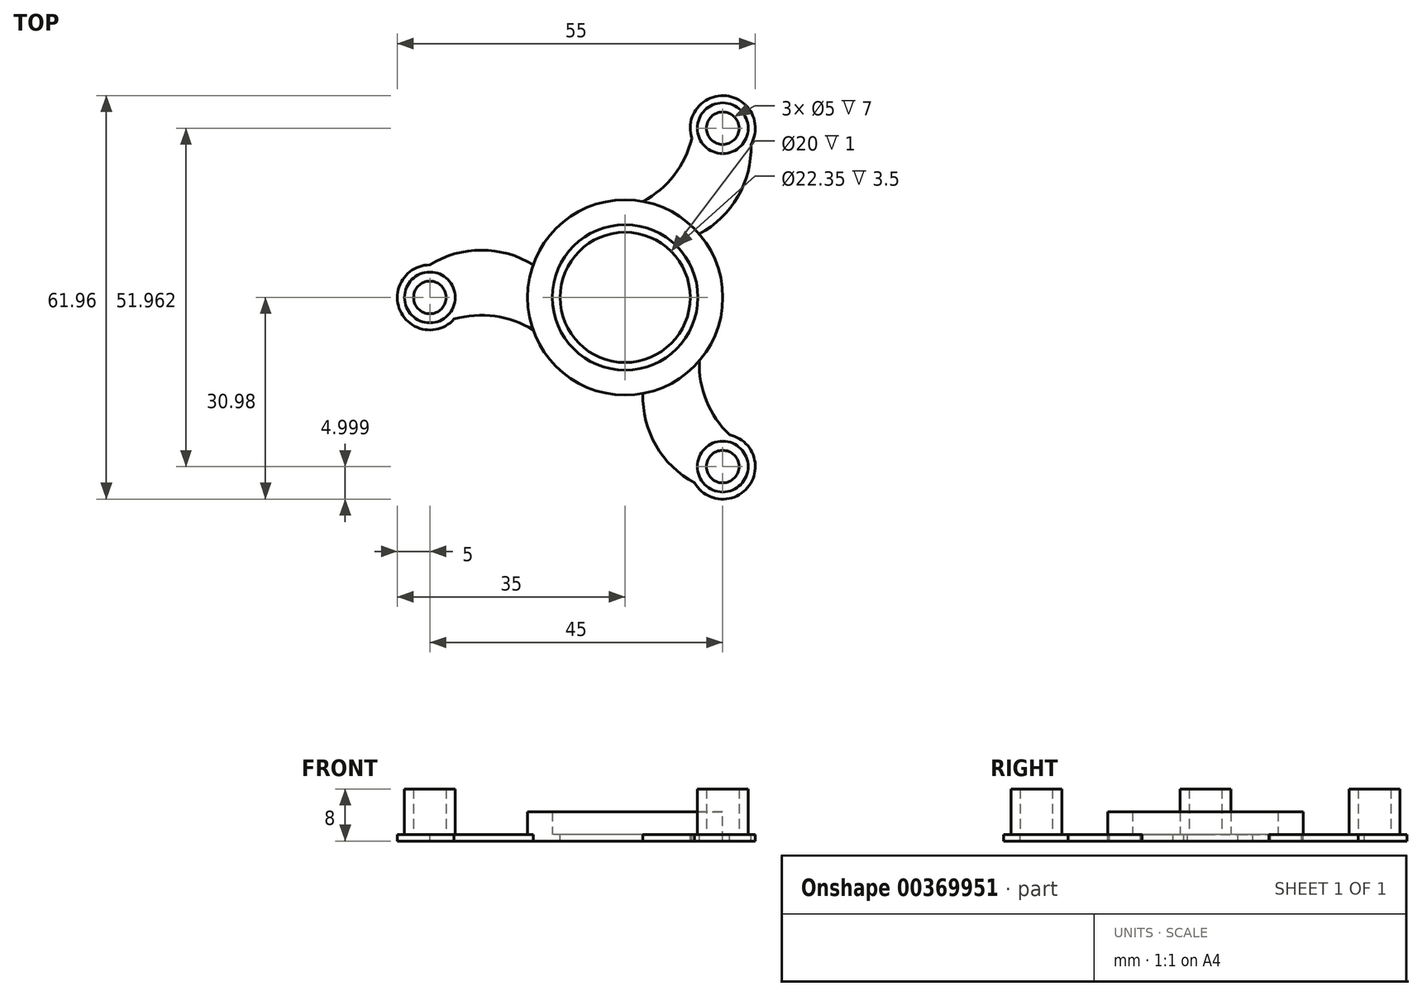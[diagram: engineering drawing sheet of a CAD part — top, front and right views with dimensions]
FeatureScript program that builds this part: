
annotation { "Feature Type Name" : "Feature", "Feature Type Description" : "" }
export const myFeature = defineFeature(function(context is Context, id is Id, definition is map)
    precondition{}
    {
        {
            var Q0;
            Q0=qCreatedBy(makeId("Top.planeOp"),FACE);
            var sketch = newSketch(context, id + "F0", { "sketchPlane" : qUnion([Q0])});
            skCircle(sketch, "E0", {"center": v(0, 0) * mm, "radius": 11.18 * mm});
            skCircle(sketch, "E1", {"center": v(-30, 0) * mm, "radius": 3.9 * mm});
            skCircle(sketch, "E2", {"center": v(-30, 0) * mm, "radius": 11.18 * mm, "construction": true});
            skCircle(sketch, "E3", {"center": v(-30, 0) * mm, "radius": 2.5 * mm});
            skCircle(sketch, "E4", {"center": v(0, 0) * mm, "radius": 15 * mm});
            skCircle(sketch, "E5", {"center": v(-30, 0) * mm, "radius": 5 * mm});
            skLineSegment(sketch, "E6", {"start": v(-30, 0) * mm, "end": v(-30, 5) * mm, "construction": true});
            skLineSegment(sketch, "E7", {"start": v(-30, 0) * mm, "end": v(-30, -5) * mm, "construction": true});
            skArc(sketch, "E8", {"start": v(-14.14, 5) * mm, "mid": v(-22.07, 7.27) * mm, "end": v(-30, 5) * mm});
            skArc(sketch, "E9", {"start": v(-14.14, -5) * mm, "mid": v(-22.07, -2.73) * mm, "end": v(-30, -5) * mm});
            skArc(sketch, "E10.1.1", {"start": v(2.74, -14.75) * mm, "mid": v(4.74, -22.75) * mm, "end": v(10.67, -28.48) * mm});
            skArc(sketch, "E10.1.2", {"start": v(11.4, -9.75) * mm, "mid": v(13.4, -17.75) * mm, "end": v(19.33, -23.48) * mm});
            skCircle(sketch, "E10.1.3", {"center": v(15, -25.98) * mm, "radius": 5 * mm});
            skCircle(sketch, "E10.1.4", {"center": v(15, -25.98) * mm, "radius": 3.9 * mm});
            skCircle(sketch, "E10.1.5", {"center": v(15, -25.98) * mm, "radius": 2.5 * mm});
            skLineSegment(sketch, "E10.1.6", {"start": v(15, -25.98) * mm, "end": v(19.33, -23.48) * mm, "construction": true});
            skLineSegment(sketch, "E10.1.7", {"start": v(15, -25.98) * mm, "end": v(10.67, -28.48) * mm, "construction": true});
            skArc(sketch, "E10.2.1", {"start": v(11.4, 9.75) * mm, "mid": v(17.33, 15.48) * mm, "end": v(19.33, 23.48) * mm});
            skArc(sketch, "E10.2.2", {"start": v(2.74, 14.75) * mm, "mid": v(8.67, 20.48) * mm, "end": v(10.67, 28.48) * mm});
            skCircle(sketch, "E10.2.3", {"center": v(15, 25.98) * mm, "radius": 5 * mm});
            skCircle(sketch, "E10.2.4", {"center": v(15, 25.98) * mm, "radius": 3.9 * mm});
            skCircle(sketch, "E10.2.5", {"center": v(15, 25.98) * mm, "radius": 2.5 * mm});
            skLineSegment(sketch, "E10.2.6", {"start": v(15, 25.98) * mm, "end": v(10.67, 28.48) * mm, "construction": true});
            skLineSegment(sketch, "E10.2.7", {"start": v(15, 25.98) * mm, "end": v(19.33, 23.48) * mm, "construction": true});
            skCircle(sketch, "E11", {"center": v(0, 0) * mm, "radius": 10 * mm});
            skSolve(sketch);
        }
        {
            var Q0;
            Q0=makeQuery(id+"F0.imprint","IMPRINT",FACE,{"disambiguationData":[TD([[makeQuery(id+"F0.imprint","IMPRINT",EDGE,{"derivedFrom":sQuery(id+"F0.wireOp",EDGE,"E1")}),-1.0]])]});
            var Q1;
            Q1=makeQuery(id+"F0.imprint","IMPRINT",FACE,{"disambiguationData":[TD([[makeQuery(id+"F0.imprint","IMPRINT",EDGE,{"derivedFrom":sQuery(id+"F0.wireOp",EDGE,"E1")}),1.0]])]});
            var Q2;
            Q2=makeQuery(id+"F0.imprint","IMPRINT",FACE,{"disambiguationData":[TD([[makeQuery(id+"F0.imprint","IMPRINT",EDGE,{"derivedFrom":sQuery(id+"F0.wireOp",EDGE,"E3")}),1.0]])]});
            var Q3;
            {var subQ0=sQuery(id+"F0.wireOp",EDGE,"E9");var subQ1=sQuery(id+"F0.wireOp",EDGE,"E5");var subQ2=makeQuery(id+"F0.imprint","INTERSECT",VERTEX,{"disambiguationData":[OD(0.0)],"derivedFrom":[subQ1,subQ0]});Q3=makeQuery(id+"F0.imprint","IMPRINT",FACE,{"disambiguationData":[TD([[makeQuery(id+"F0.imprint","IMPRINT",EDGE,{"disambiguationData":[TD([[subQ2,-1.0]])],"derivedFrom":subQ1}),1.0]])]});}
            var Q4;
            Q4=makeQuery(id+"F0.imprint","IMPRINT",FACE,{"disambiguationData":[TD([[makeQuery(id+"F0.imprint","IMPRINT",EDGE,{"derivedFrom":sQuery(id+"F0.wireOp",EDGE,"E10.1.4")}),-1.0]])]});
            var Q5;
            {var subQ0=sQuery(id+"F0.wireOp",EDGE,"E10.1.3");var subQ1=sQuery(id+"F0.wireOp",EDGE,"E10.1.2");var subQ2=makeQuery(id+"F0.imprint","INTERSECT",VERTEX,{"disambiguationData":[OD(0.0)],"derivedFrom":[subQ1,subQ0]});Q5=makeQuery(id+"F0.imprint","IMPRINT",FACE,{"disambiguationData":[TD([[makeQuery(id+"F0.imprint","IMPRINT",EDGE,{"disambiguationData":[TD([[subQ2,1.0]])],"derivedFrom":subQ1}),1.0]])]});}
            var Q6;
            Q6=makeQuery(id+"F0.imprint","IMPRINT",FACE,{"disambiguationData":[TD([[makeQuery(id+"F0.imprint","IMPRINT",EDGE,{"derivedFrom":sQuery(id+"F0.wireOp",EDGE,"E10.1.5")}),1.0]])]});
            var Q7;
            Q7=makeQuery(id+"F0.imprint","IMPRINT",FACE,{"disambiguationData":[TD([[makeQuery(id+"F0.imprint","IMPRINT",EDGE,{"derivedFrom":sQuery(id+"F0.wireOp",EDGE,"E10.1.4")}),1.0]])]});
            var Q8;
            Q8=makeQuery(id+"F0.imprint","IMPRINT",FACE,{"disambiguationData":[TD([[makeQuery(id+"F0.imprint","IMPRINT",EDGE,{"derivedFrom":sQuery(id+"F0.wireOp",EDGE,"E10.2.4")}),-1.0]])]});
            var Q9;
            Q9=makeQuery(id+"F0.imprint","IMPRINT",FACE,{"disambiguationData":[TD([[makeQuery(id+"F0.imprint","IMPRINT",EDGE,{"derivedFrom":sQuery(id+"F0.wireOp",EDGE,"E10.2.5")}),1.0]])]});
            var Q10;
            Q10=makeQuery(id+"F0.imprint","IMPRINT",FACE,{"disambiguationData":[TD([[makeQuery(id+"F0.imprint","IMPRINT",EDGE,{"derivedFrom":sQuery(id+"F0.wireOp",EDGE,"E10.2.4")}),1.0]])]});
            var Q11;
            {var subQ0=sQuery(id+"F0.wireOp",EDGE,"E10.2.3");var subQ1=sQuery(id+"F0.wireOp",EDGE,"E10.2.2");var subQ2=makeQuery(id+"F0.imprint","INTERSECT",VERTEX,{"disambiguationData":[OD(0.0)],"derivedFrom":[subQ1,subQ0]});Q11=makeQuery(id+"F0.imprint","IMPRINT",FACE,{"disambiguationData":[TD([[makeQuery(id+"F0.imprint","IMPRINT",EDGE,{"disambiguationData":[TD([[subQ2,1.0]])],"derivedFrom":subQ1}),1.0]])]});}
            var Q12;
            {var subQ0=sQuery(id+"F0.wireOp",EDGE,"E8");Q12=makeQuery(id+"F0.imprint","IMPRINT",FACE,{"disambiguationData":[TD([[makeQuery(id+"F0.imprint","IMPRINT",EDGE,{"derivedFrom":subQ0}),1.0]])]});}
            var Q13;
            {var subQ0=sQuery(id+"F0.wireOp",EDGE,"E10.2.1");Q13=makeQuery(id+"F0.imprint","IMPRINT",FACE,{"disambiguationData":[TD([[makeQuery(id+"F0.imprint","IMPRINT",EDGE,{"derivedFrom":subQ0}),1.0]])]});}
            var Q14;
            Q14=makeQuery(id+"F0.imprint","IMPRINT",FACE,{"disambiguationData":[TD([[makeQuery(id+"F0.imprint","IMPRINT",EDGE,{"derivedFrom":sQuery(id+"F0.wireOp",EDGE,"E0")}),-1.0]])]});
            var Q15;
            {var subQ0=sQuery(id+"F0.wireOp",EDGE,"E10.1.1");Q15=makeQuery(id+"F0.imprint","IMPRINT",FACE,{"disambiguationData":[TD([[makeQuery(id+"F0.imprint","IMPRINT",EDGE,{"derivedFrom":subQ0}),1.0]])]});}
            var Q16;
            Q16=makeQuery(id+"F0.imprint","IMPRINT",FACE,{"disambiguationData":[TD([[makeQuery(id+"F0.imprint","IMPRINT",EDGE,{"derivedFrom":sQuery(id+"F0.wireOp",EDGE,"E0")}),1.0]])]});
            extrude(context, id + "F1", {"entities" : qUnion([Q0, Q1, Q2, Q3, Q4, Q5, Q6, Q7, Q8, Q9, Q10, Q11, Q12, Q13, Q14, Q15, Q16]), "oppositeDirection" : true, "depth" : 1 * mm, "offsetDistance" : 25 * mm});
        }
        {
            var Q0;
            Q0=makeQuery(id+"F0.imprint","IMPRINT",FACE,{"disambiguationData":[TD([[makeQuery(id+"F0.imprint","IMPRINT",EDGE,{"derivedFrom":sQuery(id+"F0.wireOp",EDGE,"E1")}),1.0]])]});
            var Q1;
            Q1=makeQuery(id+"F0.imprint","IMPRINT",FACE,{"disambiguationData":[TD([[makeQuery(id+"F0.imprint","IMPRINT",EDGE,{"derivedFrom":sQuery(id+"F0.wireOp",EDGE,"E10.2.4")}),1.0]])]});
            var Q2;
            Q2=makeQuery(id+"F0.imprint","IMPRINT",FACE,{"disambiguationData":[TD([[makeQuery(id+"F0.imprint","IMPRINT",EDGE,{"derivedFrom":sQuery(id+"F0.wireOp",EDGE,"E10.1.4")}),1.0]])]});
            extrude(context, id + "F2", {"entities" : qUnion([Q0, Q1, Q2]), "operationType" : NewBodyOperationType.ADD, "depth" : 7 * mm, "offsetDistance" : 25 * mm});
        }
        {
            var Q0;
            Q0=makeQuery(id+"F0.imprint","IMPRINT",FACE,{"disambiguationData":[TD([[makeQuery(id+"F0.imprint","IMPRINT",EDGE,{"derivedFrom":sQuery(id+"F0.wireOp",EDGE,"E0")}),-1.0]])]});
            extrude(context, id + "F3", {"entities" : qUnion([Q0]), "operationType" : NewBodyOperationType.ADD, "depth" : 3.5 * mm, "offsetDistance" : 25 * mm});
        }
    });
